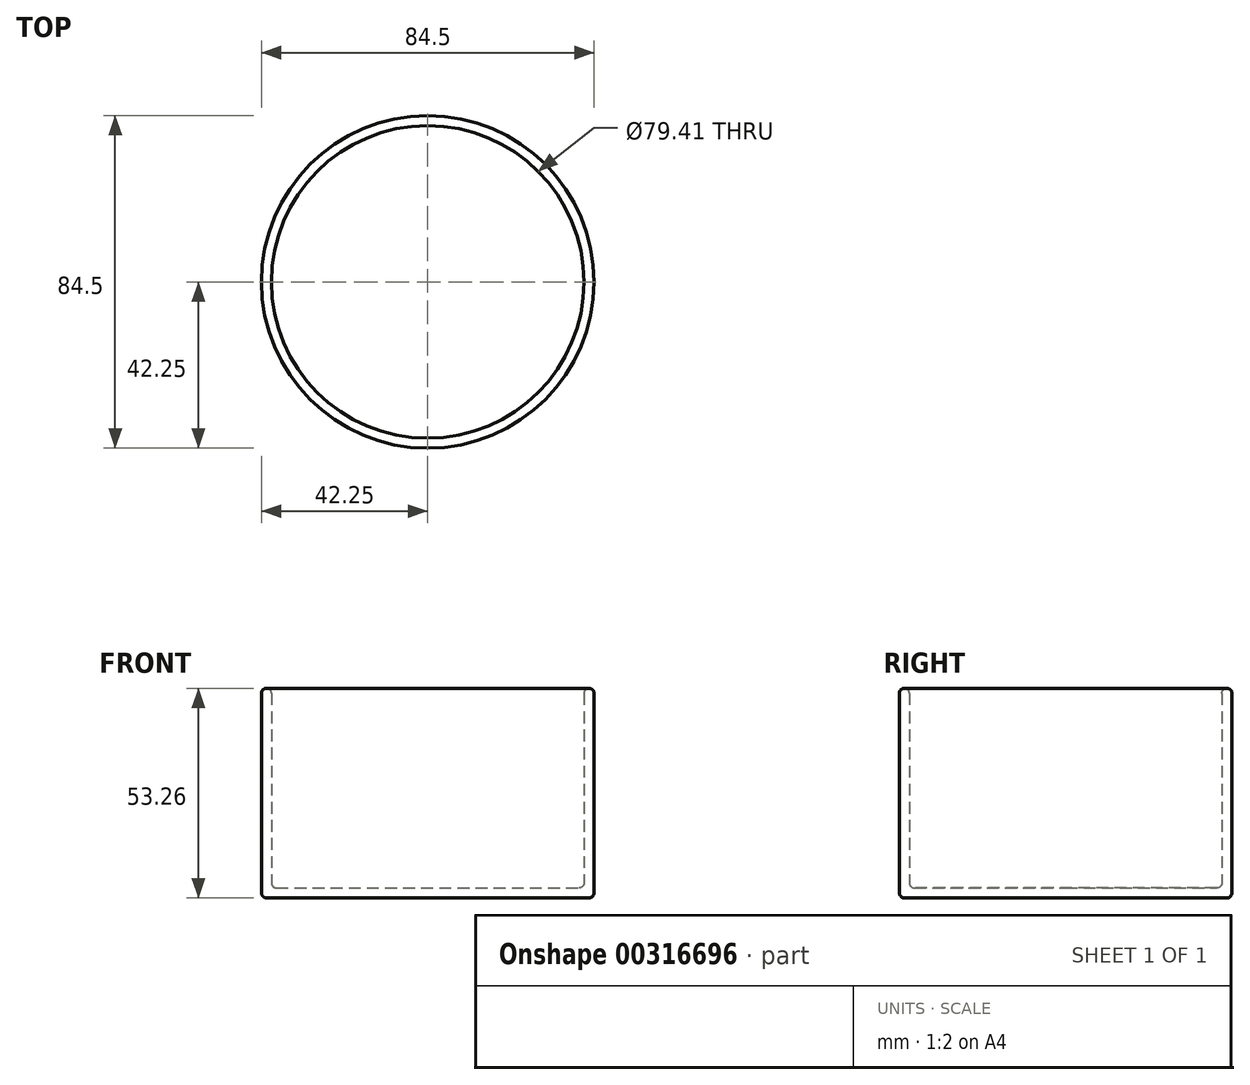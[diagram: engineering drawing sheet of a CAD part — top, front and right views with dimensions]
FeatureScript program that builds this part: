
annotation { "Feature Type Name" : "Feature", "Feature Type Description" : "" }
export const myFeature = defineFeature(function(context is Context, id is Id, definition is map)
    precondition{}
    {
        {
            var Q0;
            Q0=qCreatedBy(makeId("Front.planeOp"),FACE);
            var sketch = newSketch(context, id + "F0", { "sketchPlane" : qUnion([Q0])});
            skLineSegment(sketch, "E0", {"start": v(0, -25.48) * mm, "end": v(0, 27.78) * mm, "construction": true});
            skLineSegment(sketch, "E1", {"start": v(0, -25.48) * mm, "end": v(-42.25, -25.48) * mm});
            skLineSegment(sketch, "E2", {"start": v(-42.25, -25.48) * mm, "end": v(-42.25, 27.78) * mm});
            skLineSegment(sketch, "E3", {"start": v(-42.25, 27.78) * mm, "end": v(0, 27.78) * mm});
            skLineSegment(sketch, "E4", {"start": v(0, -25.48) * mm, "end": v(0, 27.78) * mm});
            skSolve(sketch);
        }
        {
            var Q0;
            Q0=makeQuery(id+"F0.imprint","IMPRINT",FACE,{"disambiguationData":[TD([[makeQuery(id+"F0.imprint","IMPRINT",EDGE,{"derivedFrom":sQuery(id+"F0.wireOp",EDGE,"E1")}),-1.0]])]});
            var Q1;
            Q1=sQuery(id+"F0.wireOp",EDGE,"E4");
            revolve(context, id + "F1", {"entities" : qUnion([Q0]), "axis" : qUnion([Q1]), "revolveType" : RevolveType.FULL});
        }
        {
            var Q0;
            Q0=makeQuery(id+"F1.opRevolve","SWEPT_FACE",FACE,{"disambiguationData":[OSD([sQuery(id+"F0.wireOp",EDGE,"E3")])]});
            shell(context, id + "F2", {"entities" : qUnion([Q0]), "thickness" : 2.54 * mm});
        }
        {
            var Q0;
            Q0=makeQuery(id+"F2.opShell","OFFSET_EDGE",EDGE,{"disambiguationData":[OSD([sQuery(id+"F0.wireOp",EDGE,"E2"),sQuery(id+"F0.wireOp",EDGE,"E3")])]});
            var Q1;
            Q1=makeQuery(id+"F1.opRevolve","SWEPT_EDGE",EDGE,{"disambiguationData":[OSD([sQuery(id+"F0.wireOp",EDGE,"E2"),sQuery(id+"F0.wireOp",EDGE,"E3")])]});
            fillet(context, id + "F3", {"entities" : qUnion([Q0, Q1]), "radius" : 1.27 * mm, "tangentPropagation" : true, "allowEdgeOverflow" : false});
        }
        {
            var Q0;
            Q0=makeQuery(id+"F2.opShell","OFFSET_EDGE",EDGE,{"disambiguationData":[OSD([sQuery(id+"F0.wireOp",EDGE,"E1"),sQuery(id+"F0.wireOp",EDGE,"E2")])]});
            var Q1;
            Q1=makeQuery(id+"F1.opRevolve","SWEPT_EDGE",EDGE,{"disambiguationData":[OSD([sQuery(id+"F0.wireOp",EDGE,"E1"),sQuery(id+"F0.wireOp",EDGE,"E2")])]});
            fillet(context, id + "F4", {"entities" : qUnion([Q0, Q1]), "radius" : 1.27 * mm, "tangentPropagation" : true, "allowEdgeOverflow" : false});
        }
    });
